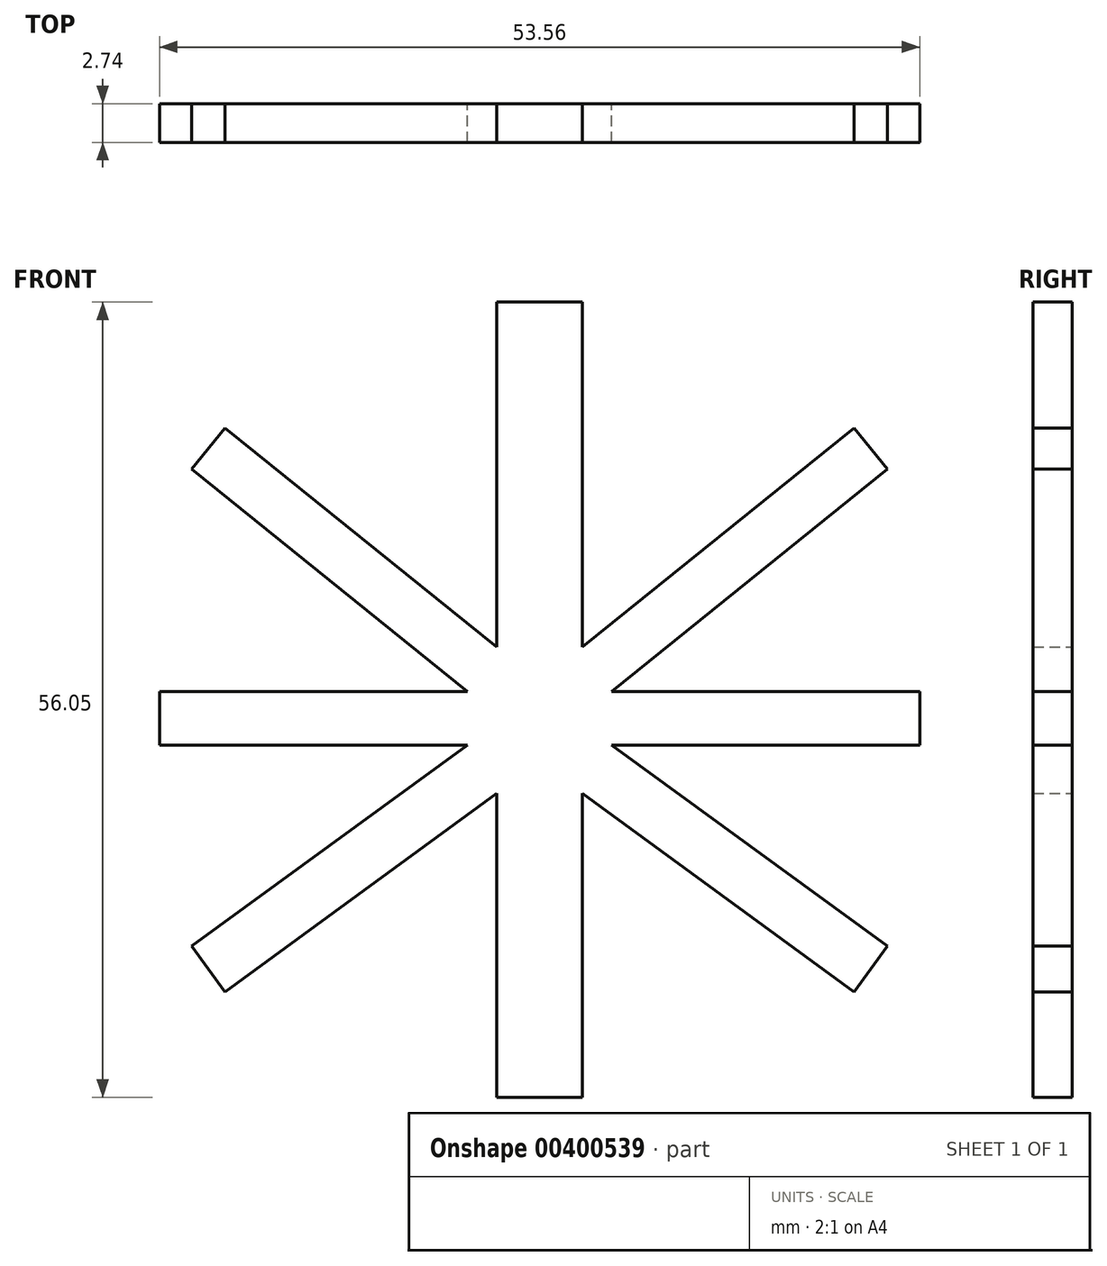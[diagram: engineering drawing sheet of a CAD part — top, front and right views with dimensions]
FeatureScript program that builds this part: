
annotation { "Feature Type Name" : "Feature", "Feature Type Description" : "" }
export const myFeature = defineFeature(function(context is Context, id is Id, definition is map)
    precondition{}
    {
        {
            var Q0;
            Q0=qCreatedBy(makeId("Front.planeOp"),FACE);
            var sketch = newSketch(context, id + "F0", { "sketchPlane" : qUnion([Q0])});
            skLineSegment(sketch, "E0", {"start": v(0, 67.4) * mm, "end": v(3.35, 67.4) * mm});
            skLineSegment(sketch, "E1", {"start": v(3.35, 67.4) * mm, "end": v(3.35, 40.4) * mm});
            skLineSegment(sketch, "E2", {"start": v(3.35, 40.4) * mm, "end": v(24.63, 57.54) * mm});
            skLineSegment(sketch, "E3", {"start": v(24.63, 57.54) * mm, "end": v(27.24, 54.3) * mm});
            skLineSegment(sketch, "E4", {"start": v(27.24, 54.3) * mm, "end": v(5.64, 36.9) * mm});
            skLineSegment(sketch, "E5", {"start": v(5.64, 36.9) * mm, "end": v(29.76, 36.9) * mm});
            skLineSegment(sketch, "E6", {"start": v(29.76, 36.9) * mm, "end": v(29.76, 32.71) * mm});
            skLineSegment(sketch, "E7", {"start": v(29.76, 32.71) * mm, "end": v(5.64, 32.71) * mm});
            skLineSegment(sketch, "E8", {"start": v(5.64, 32.71) * mm, "end": v(27.24, 16.95) * mm});
            skLineSegment(sketch, "E9", {"start": v(27.24, 16.95) * mm, "end": v(24.63, 13.38) * mm});
            skLineSegment(sketch, "E10", {"start": v(24.63, 13.38) * mm, "end": v(3.35, 28.9) * mm});
            skLineSegment(sketch, "E11", {"start": v(3.35, 28.9) * mm, "end": v(3.35, 5.12) * mm});
            skLineSegment(sketch, "E12", {"start": v(3.35, 5.12) * mm, "end": v(0, 5.12) * mm});
            skLineSegment(sketch, "E13", {"start": v(0, 67.4) * mm, "end": v(0, 5.12) * mm});
            skLineSegment(sketch, "E14.MirrorCS", {"start": v(-3.35, 40.4) * mm, "end": v(-24.63, 57.54) * mm});
            skLineSegment(sketch, "E15.MirrorCS", {"start": v(-27.24, 54.3) * mm, "end": v(-5.64, 36.9) * mm});
            skLineSegment(sketch, "E16.MirrorCS", {"start": v(-5.64, 36.9) * mm, "end": v(-29.76, 36.9) * mm});
            skLineSegment(sketch, "E17.MirrorCS", {"start": v(-29.76, 32.71) * mm, "end": v(-5.64, 32.71) * mm});
            skLineSegment(sketch, "E18.MirrorCS", {"start": v(-5.64, 32.71) * mm, "end": v(-27.24, 16.95) * mm});
            skLineSegment(sketch, "E19.MirrorCS", {"start": v(-24.63, 13.38) * mm, "end": v(-3.35, 28.9) * mm});
            skLineSegment(sketch, "E20.MirrorCS", {"start": v(-3.35, 28.9) * mm, "end": v(-3.35, 5.12) * mm});
            skLineSegment(sketch, "E21.MirrorCS", {"start": v(-27.24, 16.95) * mm, "end": v(-24.63, 13.38) * mm});
            skLineSegment(sketch, "E22.MirrorCS", {"start": v(-3.35, 5.12) * mm, "end": v(0, 5.12) * mm});
            skLineSegment(sketch, "E23.MirrorCS", {"start": v(-29.76, 36.9) * mm, "end": v(-29.76, 32.71) * mm});
            skLineSegment(sketch, "E24.MirrorCS", {"start": v(-24.63, 57.54) * mm, "end": v(-27.24, 54.3) * mm});
            skLineSegment(sketch, "E25.MirrorCS", {"start": v(-3.35, 67.4) * mm, "end": v(-3.35, 40.4) * mm});
            skLineSegment(sketch, "E26.MirrorCS", {"start": v(0, 67.4) * mm, "end": v(-3.35, 67.4) * mm});
            skSolve(sketch);
        }
        {
            var Q0;
            Q0 = qSketchRegion(id + "F0", true);
            extrude(context, id + "F1", {"entities" : qUnion([Q0]), "depth" : 3.05 * mm});
        }
        {
            var Q0;
            Q0=makeQuery(id+"F1.opExtrude","SWEPT_BODY",BODY,{"disambiguationData":[OSD([sQuery(id+"F0.wireOp",EDGE,"E0"),sQuery(id+"F0.wireOp",EDGE,"E1"),sQuery(id+"F0.wireOp",EDGE,"E2"),sQuery(id+"F0.wireOp",EDGE,"E3"),sQuery(id+"F0.wireOp",EDGE,"E4"),sQuery(id+"F0.wireOp",EDGE,"E5"),sQuery(id+"F0.wireOp",EDGE,"E6"),sQuery(id+"F0.wireOp",EDGE,"E7"),sQuery(id+"F0.wireOp",EDGE,"E8"),sQuery(id+"F0.wireOp",EDGE,"E9"),sQuery(id+"F0.wireOp",EDGE,"E10"),sQuery(id+"F0.wireOp",EDGE,"E11"),sQuery(id+"F0.wireOp",EDGE,"E12"),sQuery(id+"F0.wireOp",EDGE,"E14.MirrorCS"),sQuery(id+"F0.wireOp",EDGE,"E15.MirrorCS"),sQuery(id+"F0.wireOp",EDGE,"E16.MirrorCS"),sQuery(id+"F0.wireOp",EDGE,"E17.MirrorCS"),sQuery(id+"F0.wireOp",EDGE,"E18.MirrorCS"),sQuery(id+"F0.wireOp",EDGE,"E19.MirrorCS"),sQuery(id+"F0.wireOp",EDGE,"E20.MirrorCS"),sQuery(id+"F0.wireOp",EDGE,"E21.MirrorCS"),sQuery(id+"F0.wireOp",EDGE,"E22.MirrorCS"),sQuery(id+"F0.wireOp",EDGE,"E23.MirrorCS"),sQuery(id+"F0.wireOp",EDGE,"E24.MirrorCS"),sQuery(id+"F0.wireOp",EDGE,"E25.MirrorCS"),sQuery(id+"F0.wireOp",EDGE,"E26.MirrorCS")])]});
            var Q1;
            Q1=qCreatedBy(makeId("Origin.pointOp"),VERTEX);
            transform(context, id + "F2", {"entities" : qUnion([Q0]), "transformType" : TransformType.SCALE_UNIFORMLY, "scale" : 0.9, "scalePoint" : qUnion([Q1]), "makeCopy" : false});
        }
    });
